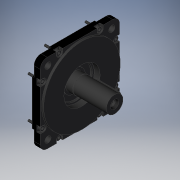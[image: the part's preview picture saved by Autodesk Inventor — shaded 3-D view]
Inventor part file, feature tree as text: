
AUTODESK INVENTOR PART (.ipt)
format: ipt  version: 2019 (Build 230136000, 136)  size: 454,656 bytes
history: native  units: mm
features: other x28, sketch x14, extrude x12, revolve x12, hole x4
ambient origin geometry x8: Origin, YZ Plane, XZ Plane, XY Plane, X Axis, Y Axis, Z Axis, Center Point
bodies: Solid1 (feature_tree)
feature tree (70):
  extrude  "Extrusion1"  Depth=2.5mm TaperAngle=0.0deg
  extrude  "Extrusion2"  TaperAngle=360.0deg  [1 undecoded]
  revolve  "Revolution1"  [1 undecoded]
  revolve  "Revolution2"  Angle=360.0deg
  revolve  "Revolution3"  Angle=360.0deg
  hole  "Hole1"  [1 undecoded]
  hole  "Hole2"  [1 undecoded]
  hole  "Hole3"  [1 undecoded]
  hole  "Hole4"  [1 undecoded]
  extrude  "Extrusion3"  Depth=4.0mm TaperAngle=0.0deg
  extrude  "Extrusion4"  Depth=4.0mm TaperAngle=0.0deg
  revolve  "Revolution4"  [1 undecoded]
  revolve  "Revolution5"  [1 undecoded]
  other  "Pattern_1_SKETCH_1"
  other  "Pattern_1_SKETCH_2"
  other  "Pattern_1_SKETCH_3"
  other  "Pattern_1_SKETCH_4"
  other  "Pattern_1_SKETCH_5"
  other  "Pattern_1_SKETCH_6"
  other  "Pattern_1_SKETCH_7"
  revolve  "Revolution6"  [1 undecoded]
  revolve  "Revolution7"  [1 undecoded]
  revolve  "Revolution8"  [1 undecoded]
  revolve  "Revolution9"  [1 undecoded]
  revolve  "Revolution10"  [1 undecoded]
  revolve  "Revolution11"  [1 undecoded]
  revolve  "Revolution12"  [1 undecoded]
  extrude  "Extrusion5"  [1 undecoded]
  other  "Pattern_3_SKETCH_1"
  other  "Pattern_3_SKETCH_2"
  other  "Pattern_3_SKETCH_3"
  other  "Pattern_3_SKETCH_4"
  other  "Pattern_3_SKETCH_5"
  other  "Pattern_3_SKETCH_6"
  other  "Pattern_3_SKETCH_7"
  extrude  "Extrusion6"  [1 undecoded]
  extrude  "Extrusion7"  [1 undecoded]
  extrude  "Extrusion8"  [1 undecoded]
  extrude  "Extrusion9"  [1 undecoded]
  extrude  "Extrusion10"  [1 undecoded]
  extrude  "Extrusion11"  [1 undecoded]
  extrude  "Extrusion12"  [1 undecoded]
  other  "F_XY"
  other  "F_YZ"
  other  "F_ZX"
  other  "F_X"
  other  "F_Y"
  other  "F_Z"
  other  "F_Center"
  other  "SH_SEAL_XY"
  other  "SH_SEAL_YZ"
  other  "SH_SEAL_ZX"
  other  "SH_SEAL_X"
  other  "SH_SEAL_Y"
  other  "SH_SEAL_Z"
  other  "SH_SEAL_Center"
  sketch  "Sketch_1"  dims[d0=9.0mm d1=0.0mm d2=2.5mm d3=0.0mm]
  sketch  "Sketch_2"  dims[d4=360.0deg d5=360.0deg]
  sketch  "Sketch_3"  dims[d6=360.0deg]
  sketch  "Sketch_4"  dims[d7=9.0mm d8=6.0mm d9=4.0mm d10=2.0mm d11=90.0deg d12=9.0mm d13=0.0mm]
  sketch  "Sketch_5"  dims[d14=9.0mm d15=6.0mm d16=4.0mm d17=2.0mm d18=90.0deg d19=9.0mm d20=0.0mm]
  sketch  "Sketch6"  dims[d21=9.0mm d22=6.0mm d23=4.0mm d24=2.0mm d25=90.0deg d26=9.0mm d27=0.0mm]
  sketch  "Sketch7"  dims[d37=4.0mm d38=0.0mm d39=360.0deg]
  sketch  "Sketch8"  dims[d40=360.0deg d41=360.0deg]
  sketch  "Sketch9"  dims[d42=360.0deg d43=360.0deg]
  sketch  "Sketch_11"  dims[d44=360.0deg d45=360.0deg]
  sketch  "Sketch_17"  dims[d48=4.0mm d49=0.0mm d50=4.0mm d51=0.0mm]
  sketch  "Sketch_6"  dims[d28=9.0mm d29=6.0mm d30=4.0mm d31=2.0mm d32=90.0deg d33=9.0mm d34=0.0mm d35=5.0mm d36=0.0mm]
  sketch  "Sketch_12"  dims[d46=360.0deg d47=360.0deg]
  sketch  "Sketch_26"  dims[d52=4.0mm d53=0.0mm d54=4.0mm d55=0.0mm d56=4.0mm d57=0.0mm d58=4.0mm d59=0.0mm d60=4.0mm d61=0.0mm d62=4.0mm d63=0.0mm d64=0.0mm d65=0.0mm]
note: 23 required parameter values undecoded (feature->parameter linkage not recoverable at this tier; creation-order binding heuristic only, values carry confidence <= 0.55)